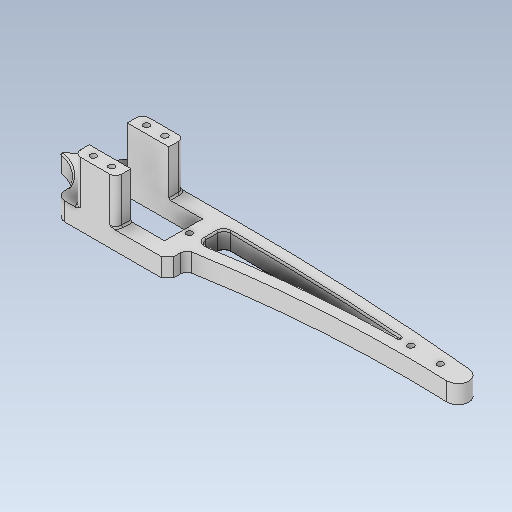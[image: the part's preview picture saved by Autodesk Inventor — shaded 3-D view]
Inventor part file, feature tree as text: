
AUTODESK INVENTOR PART (.ipt)
format: ipt  version: 2020.3 (Build 243373000, 373)  size: 335,360 bytes
history: native  units: mm
features: fillet x7, hole x3, sketch x2, extrude x2, chamfer x1
ambient origin geometry x8: Origin, YZ Plane, XZ Plane, XY Plane, X Axis, Y Axis, Z Axis, Center Point
bodies: Solid1 (feature_tree)
feature tree (15):
  sketch  "Sketch1"  dims[d4=6.0mm d5=24.6mm d6=12.4mm d7=5.0mm d15=7.0mm]
  extrude  "Extrusion1"  Depth=24.6mm
  fillet  "Fillet1"  Radius=12.4mm
  fillet  "Fillet2"  Radius=5.0mm
  fillet  "Fillet3"  Radius=7.0mm
  hole  "Hole1"  [1 undecoded]
  fillet  "Fillet4"  Radius=20.0mm
  hole  "Hole2"  [1 undecoded]
  extrude  "Extrusion3"  Depth=10.0mm
  sketch  "Sketch3"  dims[d17=6.0mm d18=4.0mm d21=20.0mm d23=80.0mm d24=15.0mm d29=29.670597mm d30=6.0mm d31=10.0mm d33=6.0mm d34=0.0mm d40=3.0mm d41=3.0mm d42=2.0mm d43=4.0mm d44=3.0mm d45=4.0mm d50=13.0mm d51=12.0mm d52=22.68928mm d53=16.057029mm d54=2.0mm d55=50.8mm d56=4.0mm d57=2.0mm d58=90.0deg d59=8.0mm d60=20.594885mm d61=0.5mm d62=2.0mm d63=4.0mm d64=4.0mm d65=2.0mm d66=90.0deg d67=8.0mm d68=20.594885mm d69=20.92mm d70=0.0mm d71=2.0mm d80=2.0mm d81=2.0mm d82=45.0deg d87=0.5mm d88=0.5mm d89=6.8mm d90=28.4mm d91=6.0mm d99=2.0mm d100=6.0mm d101=4.0mm d102=2.0mm d103=90.0deg d104=10.0mm d105=20.594885mm]
  hole  "Hole5"  [1 undecoded]
  fillet  "Fillet5"  Radius=6.0mm
  chamfer  "Chamfer2"  Distance=10.0mm
  fillet  "Fillet8"  Radius=6.0mm
  fillet  "Fillet9"  Radius=3.0mm
note: 3 required parameter values undecoded (feature->parameter linkage not recoverable at this tier; creation-order binding heuristic only, values carry confidence <= 0.55)
